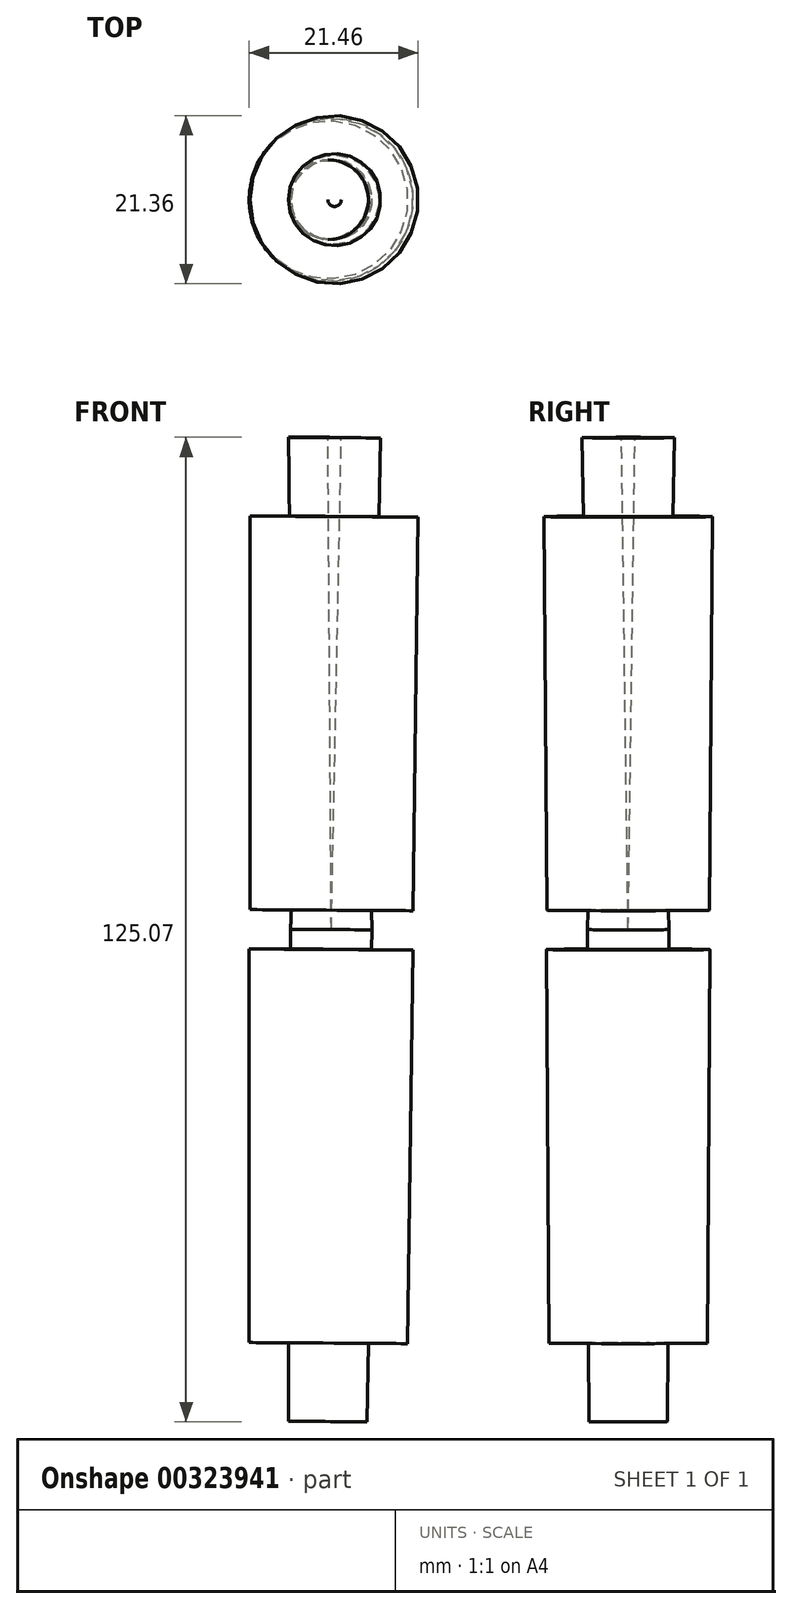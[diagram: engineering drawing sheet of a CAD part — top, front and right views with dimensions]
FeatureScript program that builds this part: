
annotation { "Feature Type Name" : "Feature", "Feature Type Description" : "" }
export const myFeature = defineFeature(function(context is Context, id is Id, definition is map)
    precondition{}
    {
        {
            var Q0;
            Q0=qCreatedBy(makeId("Front.planeOp"),FACE);
            var sketch = newSketch(context, id + "F0", { "sketchPlane" : qUnion([Q0])});
            skLineSegment(sketch, "E0", {"start": v(-4.75, 0) * mm, "end": v(-4.64, 2.5) * mm});
            skLineSegment(sketch, "E1", {"start": v(-4.64, 2.5) * mm, "end": v(-9.9, 2.5) * mm});
            skLineSegment(sketch, "E2", {"start": v(-9.9, 2.5) * mm, "end": v(-9.9, 52.5) * mm});
            skLineSegment(sketch, "E3", {"start": v(-9.9, 52.5) * mm, "end": v(-4.9, 52.5) * mm});
            skLineSegment(sketch, "E4", {"start": v(-4.9, 52.5) * mm, "end": v(-5, 62.5) * mm});
            skLineSegment(sketch, "E5", {"start": v(-5, 62.5) * mm, "end": v(0, 62.5) * mm});
            skLineSegment(sketch, "E6", {"start": v(0, 62.5) * mm, "end": v(0.43, 0) * mm});
            skLineSegment(sketch, "E7", {"start": v(-4.75, 0) * mm, "end": v(-4.75, -2.5) * mm});
            skLineSegment(sketch, "E8", {"start": v(-4.75, -2.5) * mm, "end": v(-10, -2.5) * mm});
            skLineSegment(sketch, "E9", {"start": v(-10, -2.5) * mm, "end": v(-10, -52.5) * mm});
            skLineSegment(sketch, "E10", {"start": v(-10, -52.5) * mm, "end": v(-5, -52.5) * mm});
            skLineSegment(sketch, "E11", {"start": v(-5, -52.5) * mm, "end": v(-5, -62.5) * mm});
            skLineSegment(sketch, "E12", {"start": v(-5, -62.5) * mm, "end": v(0, -62.5) * mm});
            skLineSegment(sketch, "E13", {"start": v(0, -62.5) * mm, "end": v(0.43, 0) * mm});
            skSolve(sketch);
        }
        {
            var Q0;
            Q0=makeQuery(id+"F0.imprint","IMPRINT",FACE,{"disambiguationData":[TD([[makeQuery(id+"F0.imprint","IMPRINT",EDGE,{"derivedFrom":sQuery(id+"F0.wireOp",EDGE,"E0")}),-1.0]])]});
            var Q1;
            Q1=sQuery(id+"F0.wireOp",EDGE,"E13");
            revolve(context, id + "F1", {"entities" : qUnion([Q0]), "axis" : qUnion([Q1]), "revolveType" : RevolveType.FULL});
        }
    });
